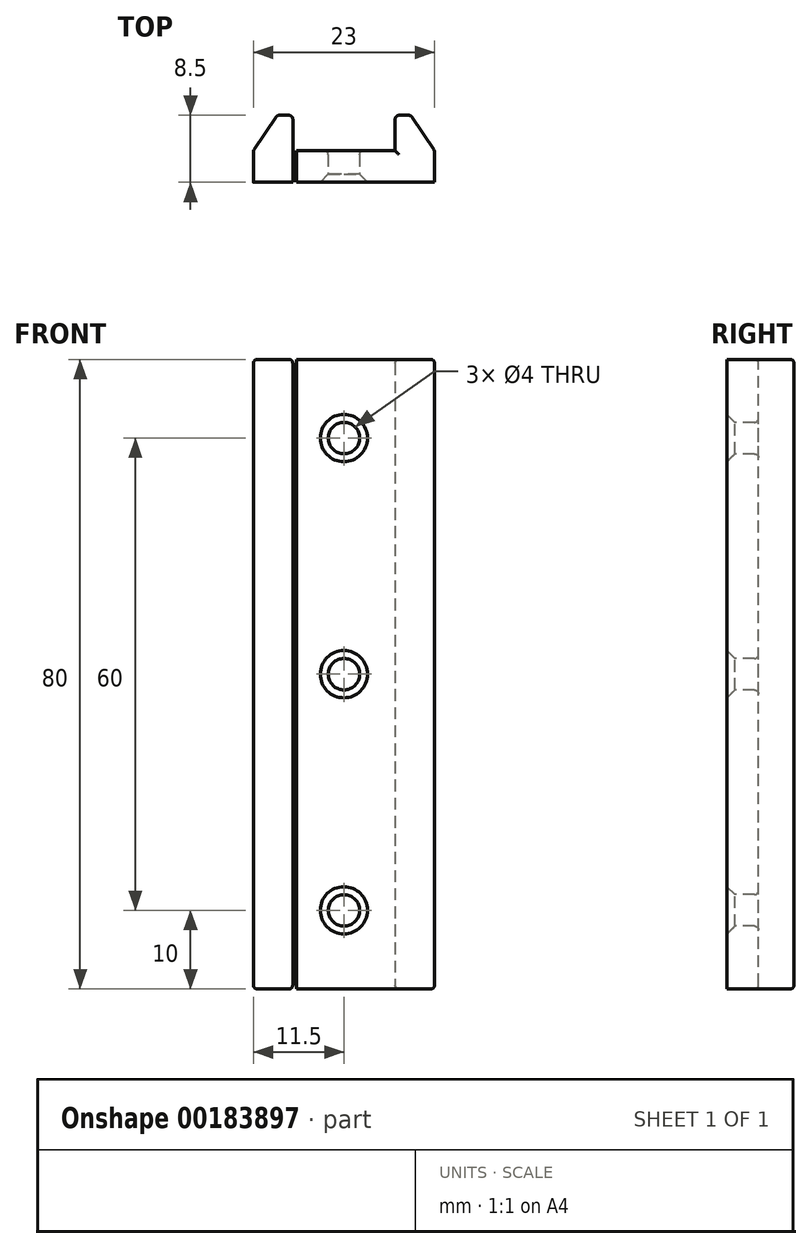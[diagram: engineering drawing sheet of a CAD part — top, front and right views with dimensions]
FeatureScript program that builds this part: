
annotation { "Feature Type Name" : "Feature", "Feature Type Description" : "" }
export const myFeature = defineFeature(function(context is Context, id is Id, definition is map)
    precondition{}
    {
        {
            var Q0;
            Q0=qCreatedBy(makeId("Front.planeOp"),FACE);
            var sketch = newSketch(context, id + "F0", { "sketchPlane" : qUnion([Q0])});
            skLineSegment(sketch, "E0.bottom", {"start": v(6, -40) * mm, "end": v(-6, -40) * mm});
            skLineSegment(sketch, "E0.top", {"start": v(6, 40) * mm, "end": v(-6, 40) * mm});
            skLineSegment(sketch, "E0.left", {"start": v(6, -40) * mm, "end": v(6, 40) * mm});
            skLineSegment(sketch, "E0.right", {"start": v(-6, -40) * mm, "end": v(-6, 40) * mm});
            skPoint(sketch, "E0.middle", {"position": v(0, 0) * mm});
            skLineSegment(sketch, "E1.bottom", {"start": v(-6, 40) * mm, "end": v(-11.5, 40) * mm});
            skLineSegment(sketch, "E1.top", {"start": v(-6, -40) * mm, "end": v(-11.5, -40) * mm});
            skLineSegment(sketch, "E1.left", {"start": v(-6, 40) * mm, "end": v(-6, -40) * mm});
            skLineSegment(sketch, "E1.right", {"start": v(-11.5, 40) * mm, "end": v(-11.5, -40) * mm});
            skLineSegment(sketch, "E2.MirrorCS", {"start": v(6.5, 40) * mm, "end": v(11.5, 40) * mm});
            skLineSegment(sketch, "E3.MirrorCS", {"start": v(11.5, 40) * mm, "end": v(11.5, -40) * mm});
            skLineSegment(sketch, "E4.MirrorCS", {"start": v(6.5, -40) * mm, "end": v(11.5, -40) * mm});
            skLineSegment(sketch, "E5.0", {"start": v(-6.5, 40) * mm, "end": v(-6.5, -40) * mm});
            skLineSegment(sketch, "E6.MirrorCS", {"start": v(6.5, 40) * mm, "end": v(6.5, -40) * mm});
            skLineSegment(sketch, "E7", {"start": v(0, 40) * mm, "end": v(0, -40) * mm, "construction": true});
            skLineSegment(sketch, "E8", {"start": v(-11.5, -30) * mm, "end": v(11.5, -30) * mm, "construction": true});
            skLineSegment(sketch, "E9", {"start": v(-11.5, 0) * mm, "end": v(11.5, 0) * mm, "construction": true});
            skCircle(sketch, "E10", {"center": v(0, 0) * mm, "radius": 2 * mm});
            skCircle(sketch, "E11", {"center": v(0, -30) * mm, "radius": 2 * mm});
            skLineSegment(sketch, "E12", {"start": v(6.5, 40) * mm, "end": v(6, 40) * mm});
            skLineSegment(sketch, "E13", {"start": v(6.5, -40) * mm, "end": v(6, -40) * mm});
            skLineSegment(sketch, "E14", {"start": v(-11.5, 30) * mm, "end": v(11.5, 30) * mm, "construction": true});
            skCircle(sketch, "E15", {"center": v(0, 30) * mm, "radius": 2 * mm});
            skSolve(sketch);
        }
        {
            var Q0;
            Q0=makeQuery(id+"F0.imprint","IMPRINT",FACE,{"disambiguationData":[TD([[makeQuery(id+"F0.imprint","IMPRINT",EDGE,{"derivedFrom":sQuery(id+"F0.wireOp",EDGE,"E0.bottom")}),-1.0]])]});
            var Q1;
            {var subQ1=sQuery(id+"F0.wireOp",EDGE,"E1.right");Q1=makeQuery(id+"F0.imprint","IMPRINT",FACE,{"disambiguationData":[TD([[makeQuery(id+"F0.imprint","IMPRINT",EDGE,{"derivedFrom":subQ1}),1.0]])]});}
            var Q2;
            {var subQ0=sQuery(id+"F0.wireOp",EDGE,"E1.left");Q2=makeQuery(id+"F0.imprint","IMPRINT",FACE,{"disambiguationData":[TD([[makeQuery(id+"F0.imprint","IMPRINT",EDGE,{"derivedFrom":subQ0}),-1.0]])]});}
            var Q3;
            Q3=makeQuery(id+"F0.imprint","IMPRINT",FACE,{"disambiguationData":[TD([[makeQuery(id+"F0.imprint","IMPRINT",EDGE,{"derivedFrom":sQuery(id+"F0.wireOp",EDGE,"E0.left")}),-1.0]])]});
            var Q4;
            Q4=makeQuery(id+"F0.imprint","IMPRINT",FACE,{"disambiguationData":[TD([[makeQuery(id+"F0.imprint","IMPRINT",EDGE,{"derivedFrom":sQuery(id+"F0.wireOp",EDGE,"E2.MirrorCS")}),-1.0]])]});
            extrude(context, id + "F1", {"entities" : qUnion([Q0, Q1, Q2, Q3, Q4]), "oppositeDirection" : true, "depth" : 4 * mm});
        }
        {
            var Q0;
            {var subQ0=sQuery(id+"F0.wireOp",EDGE,"E1.right");Q0=makeQuery(id+"F0.imprint","IMPRINT",FACE,{"disambiguationData":[TD([[makeQuery(id+"F0.imprint","IMPRINT",EDGE,{"derivedFrom":subQ0}),1.0]])]});}
            var Q1;
            {var subQ0=sQuery(id+"F0.wireOp",EDGE,"E3.MirrorCS");Q1=makeQuery(id+"F0.imprint","IMPRINT",FACE,{"disambiguationData":[TD([[makeQuery(id+"F0.imprint","IMPRINT",EDGE,{"derivedFrom":subQ0}),-1.0]])]});}
            extrude(context, id + "F2", {"entities" : qUnion([Q0, Q1]), "operationType" : NewBodyOperationType.ADD, "oppositeDirection" : true, "depth" : 8.5 * mm});
        }
        {
            var Q0;
            Q0=makeQuery(id+"F2.opExtrude","CAP_EDGE",EDGE,{"disambiguationData":[OSD([sQuery(id+"F0.wireOp",EDGE,"E1.right")])],"isStart":false});
            chamfer(context, id + "F3", {"entities" : qUnion([Q0]), "chamferType" : ChamferType.TWO_OFFSETS, "width1" : 4.5 * mm, "oppositeDirection" : false, "width2" : 3 * mm});
        }
        {
            var Q0;
            Q0=makeQuery(id+"F2.opExtrude","CAP_EDGE",EDGE,{"disambiguationData":[OSD([sQuery(id+"F0.wireOp",EDGE,"E3.MirrorCS")])],"isStart":false});
            chamfer(context, id + "F4", {"entities" : qUnion([Q0]), "chamferType" : ChamferType.TWO_OFFSETS, "width1" : 4.5 * mm, "oppositeDirection" : true, "width2" : 3 * mm, "tangentPropagation" : true});
        }
        {
            var Q0;
            Q0=sQuery(id+"F0.wireOp",VERTEX,"E10.center");
            var Q1;
            Q1=sQuery(id+"F0.wireOp",VERTEX,"E11.center");
            var Q2;
            Q2=sQuery(id+"F0.wireOp",VERTEX,"E15.center");
            var Q3;
            Q3=makeQuery(id+"F1.opExtrude","SWEPT_BODY",BODY,{"disambiguationData":[OSD([sQuery(id+"F0.wireOp",EDGE,"E0.bottom"),sQuery(id+"F0.wireOp",EDGE,"E0.top"),sQuery(id+"F0.wireOp",EDGE,"E1.bottom"),sQuery(id+"F0.wireOp",EDGE,"E1.top"),sQuery(id+"F0.wireOp",EDGE,"E1.right"),sQuery(id+"F0.wireOp",EDGE,"E2.MirrorCS"),sQuery(id+"F0.wireOp",EDGE,"E3.MirrorCS"),sQuery(id+"F0.wireOp",EDGE,"E4.MirrorCS"),sQuery(id+"F0.wireOp",EDGE,"E10"),sQuery(id+"F0.wireOp",EDGE,"E11"),sQuery(id+"F0.wireOp",EDGE,"E12"),sQuery(id+"F0.wireOp",EDGE,"E13")])]});
            hole(context, id + "F5", {"style" : HoleStyle.C_SINK, "endStyle" : HoleEndStyle.THROUGH, "holeDiameter" : 4 * mm, "cSinkDiameter" : 6 * mm, "cSinkAngle" : 90 * degree, "locations" : qUnion([Q0, Q1, Q2]), "scope" : qUnion([Q3]), "isTappedThrough" : true});
        }
        {
            var Q0;
            Q0=makeQuery(id+"F4.opChamfer","BLEND_FACE",FACE,{"disambiguationData":[OSD([sQuery(id+"F0.wireOp",EDGE,"E3.MirrorCS")])]});
            var Q1;
            Q1=makeQuery(id+"F2.opExtrude","CAP_FACE",FACE,{"disambiguationData":[OSD([sQuery(id+"F0.wireOp",EDGE,"E2.MirrorCS"),sQuery(id+"F0.wireOp",EDGE,"E3.MirrorCS"),sQuery(id+"F0.wireOp",EDGE,"E4.MirrorCS"),sQuery(id+"F0.wireOp",EDGE,"E6.MirrorCS")])],"isStart":false});
            var Q2;
            Q2=makeQuery(id+"F2.opExtrude","CAP_FACE",FACE,{"disambiguationData":[OSD([sQuery(id+"F0.wireOp",EDGE,"E1.bottom"),sQuery(id+"F0.wireOp",EDGE,"E1.top"),sQuery(id+"F0.wireOp",EDGE,"E1.right"),sQuery(id+"F0.wireOp",EDGE,"E5.0")])],"isStart":false});
            var Q3;
            Q3=makeQuery(id+"F3.opChamfer","BLEND_FACE",FACE,{"disambiguationData":[OSD([sQuery(id+"F0.wireOp",EDGE,"E1.right")])]});
            var Q4;
            Q4=makeQuery(id+"F1.opExtrude","CAP_EDGE",EDGE,{"disambiguationData":[OSD([sQuery(id+"F0.wireOp",EDGE,"E11")])],"isStart":false});
            var Q5;
            Q5=makeQuery(id+"F1.opExtrude","CAP_EDGE",EDGE,{"disambiguationData":[OSD([sQuery(id+"F0.wireOp",EDGE,"E10")])],"isStart":false});
            var Q6;
            Q6=makeQuery(id+"F1.opExtrude","CAP_EDGE",EDGE,{"disambiguationData":[OSD([sQuery(id+"F0.wireOp",EDGE,"E0.bottom"),sQuery(id+"F0.wireOp",EDGE,"E1.top"),sQuery(id+"F0.wireOp",EDGE,"E4.MirrorCS"),sQuery(id+"F0.wireOp",EDGE,"E13")])],"isStart":false});
            var Q7;
            Q7=makeQuery(id+"F2.opExtrude","SWEPT_EDGE",EDGE,{"disambiguationData":[OSD([sQuery(id+"F0.wireOp",EDGE,"E4.MirrorCS"),sQuery(id+"F0.wireOp",EDGE,"E6.MirrorCS"),sQuery(id+"F0.wireOp",EDGE,"E13")])]});
            var Q8;
            Q8=makeQuery(id+"F2.opExtrude","SWEPT_EDGE",EDGE,{"disambiguationData":[OSD([sQuery(id+"F0.wireOp",EDGE,"E1.top"),sQuery(id+"F0.wireOp",EDGE,"E5.0")])]});
            var Q9;
            {var subQ0=sQuery(id+"F0.wireOp",EDGE,"E1.right");var subQ1=sQuery(id+"F0.wireOp",EDGE,"E1.top");Q9=makeQuery(id+"F2.boolean.opBoolean","MERGE",EDGE,{"derivedFrom":[makeQuery(id+"F1.opExtrude","SWEPT_EDGE",EDGE,{"disambiguationData":[OSD([subQ1,subQ0])]}),makeQuery(id+"F2.opExtrude","SWEPT_EDGE",EDGE,{"disambiguationData":[OSD([subQ1,subQ0])]})]});}
            var Q10;
            {var subQ0=sQuery(id+"F0.wireOp",EDGE,"E4.MirrorCS");var subQ1=sQuery(id+"F0.wireOp",EDGE,"E3.MirrorCS");Q10=makeQuery(id+"F2.boolean.opBoolean","MERGE",EDGE,{"derivedFrom":[makeQuery(id+"F1.opExtrude","SWEPT_EDGE",EDGE,{"disambiguationData":[OSD([subQ1,subQ0])]}),makeQuery(id+"F2.opExtrude","SWEPT_EDGE",EDGE,{"disambiguationData":[OSD([subQ1,subQ0])]})]});}
            var Q11;
            {var subQ0=sQuery(id+"F0.wireOp",EDGE,"E3.MirrorCS");var subQ1=sQuery(id+"F0.wireOp",EDGE,"E2.MirrorCS");Q11=makeQuery(id+"F2.boolean.opBoolean","MERGE",EDGE,{"derivedFrom":[makeQuery(id+"F1.opExtrude","SWEPT_EDGE",EDGE,{"disambiguationData":[OSD([subQ1,subQ0])]}),makeQuery(id+"F2.opExtrude","SWEPT_EDGE",EDGE,{"disambiguationData":[OSD([subQ1,subQ0])]})]});}
            var Q12;
            Q12=makeQuery(id+"F2.opExtrude","SWEPT_EDGE",EDGE,{"disambiguationData":[OSD([sQuery(id+"F0.wireOp",EDGE,"E2.MirrorCS"),sQuery(id+"F0.wireOp",EDGE,"E6.MirrorCS"),sQuery(id+"F0.wireOp",EDGE,"E12")])]});
            var Q13;
            Q13=makeQuery(id+"F1.opExtrude","CAP_EDGE",EDGE,{"disambiguationData":[OSD([sQuery(id+"F0.wireOp",EDGE,"E0.top"),sQuery(id+"F0.wireOp",EDGE,"E1.bottom"),sQuery(id+"F0.wireOp",EDGE,"E2.MirrorCS"),sQuery(id+"F0.wireOp",EDGE,"E12")])],"isStart":false});
            var Q14;
            Q14=makeQuery(id+"F2.opExtrude","SWEPT_EDGE",EDGE,{"disambiguationData":[OSD([sQuery(id+"F0.wireOp",EDGE,"E1.bottom"),sQuery(id+"F0.wireOp",EDGE,"E5.0")])]});
            var Q15;
            {var subQ0=sQuery(id+"F0.wireOp",EDGE,"E1.right");var subQ1=sQuery(id+"F0.wireOp",EDGE,"E1.bottom");Q15=makeQuery(id+"F2.boolean.opBoolean","MERGE",EDGE,{"derivedFrom":[makeQuery(id+"F1.opExtrude","SWEPT_EDGE",EDGE,{"disambiguationData":[OSD([subQ1,subQ0])]}),makeQuery(id+"F2.opExtrude","SWEPT_EDGE",EDGE,{"disambiguationData":[OSD([subQ1,subQ0])]})]});}
            var Q16;
            Q16=makeQuery(id+"F1.opExtrude","CAP_EDGE",EDGE,{"disambiguationData":[OSD([sQuery(id+"F0.wireOp",EDGE,"E15")])],"isStart":false});
            fillet(context, id + "F6", {"entities" : qUnion([Q0, Q1, Q2, Q3, Q4, Q5, Q6, Q7, Q8, Q9, Q10, Q11, Q12, Q13, Q14, Q15, Q16]), "radius" : 0.5 * mm, "tangentPropagation" : true, "allowEdgeOverflow" : false});
        }
    });
